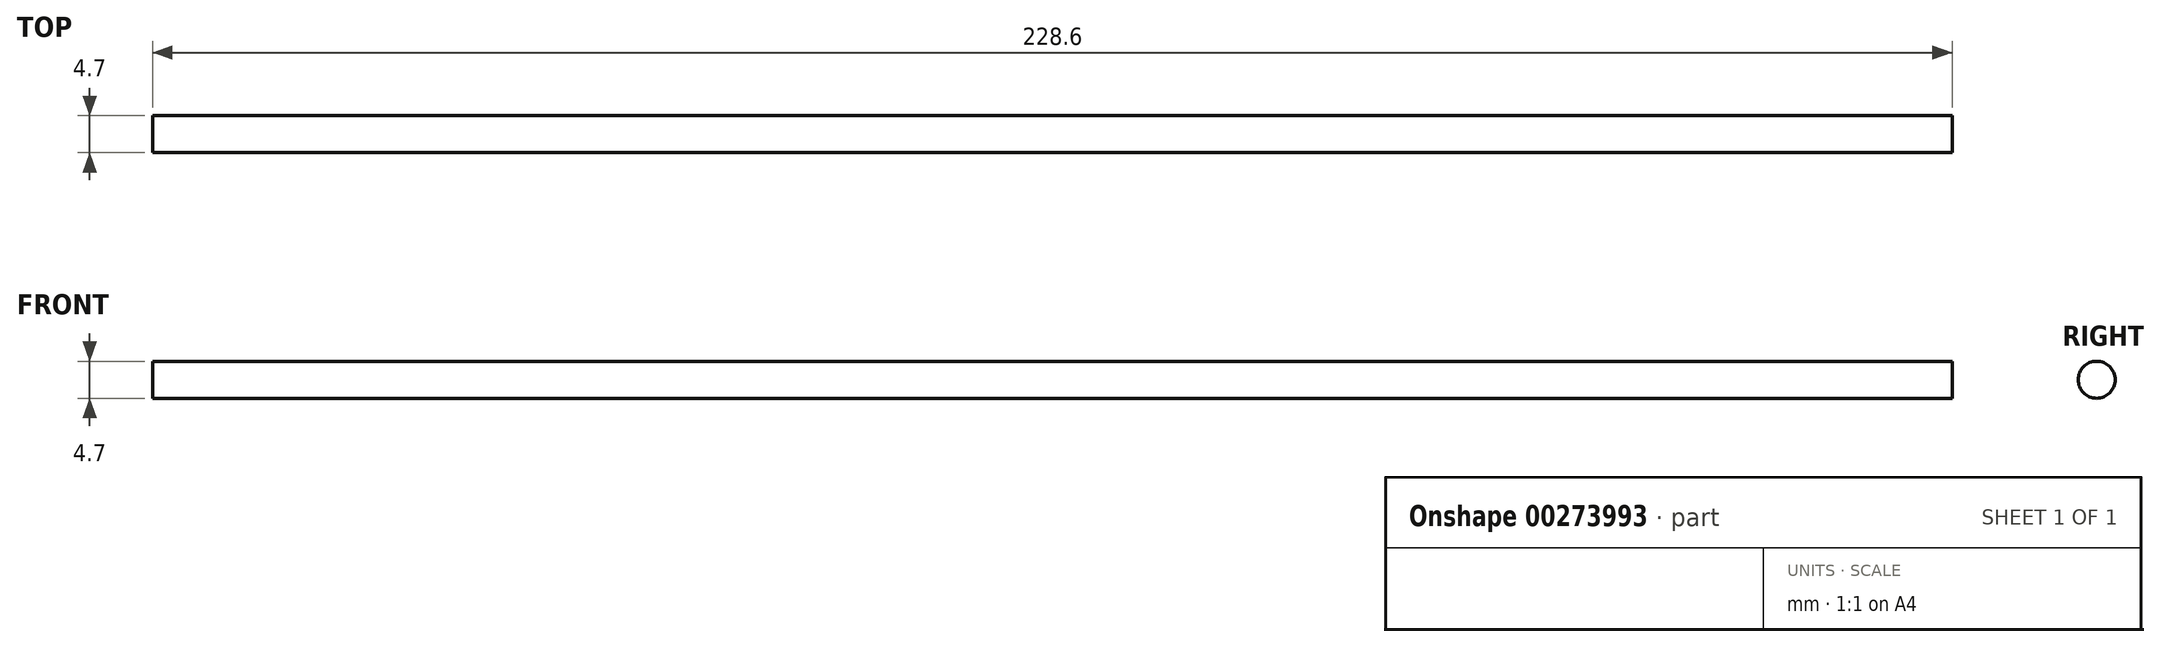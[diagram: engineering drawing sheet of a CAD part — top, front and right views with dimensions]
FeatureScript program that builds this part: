
annotation { "Feature Type Name" : "Feature", "Feature Type Description" : "" }
export const myFeature = defineFeature(function(context is Context, id is Id, definition is map)
    precondition{}
    {
        {
            var Q0;
            Q0=qCreatedBy(makeId("Right.planeOp"),FACE);
            var sketch = newSketch(context, id + "F0", { "sketchPlane" : qUnion([Q0])});
            skCircle(sketch, "E0", {"center": v(-132.6, 24.58) * mm, "radius": 2.35 * mm});
            skSolve(sketch);
        }
        {
            var Q0;
            Q0 = qSketchRegion(id + "F0", true);
            extrude(context, id + "F1", {"entities" : qUnion([Q0]), "depth" : 228.6 * mm});
        }
    });
